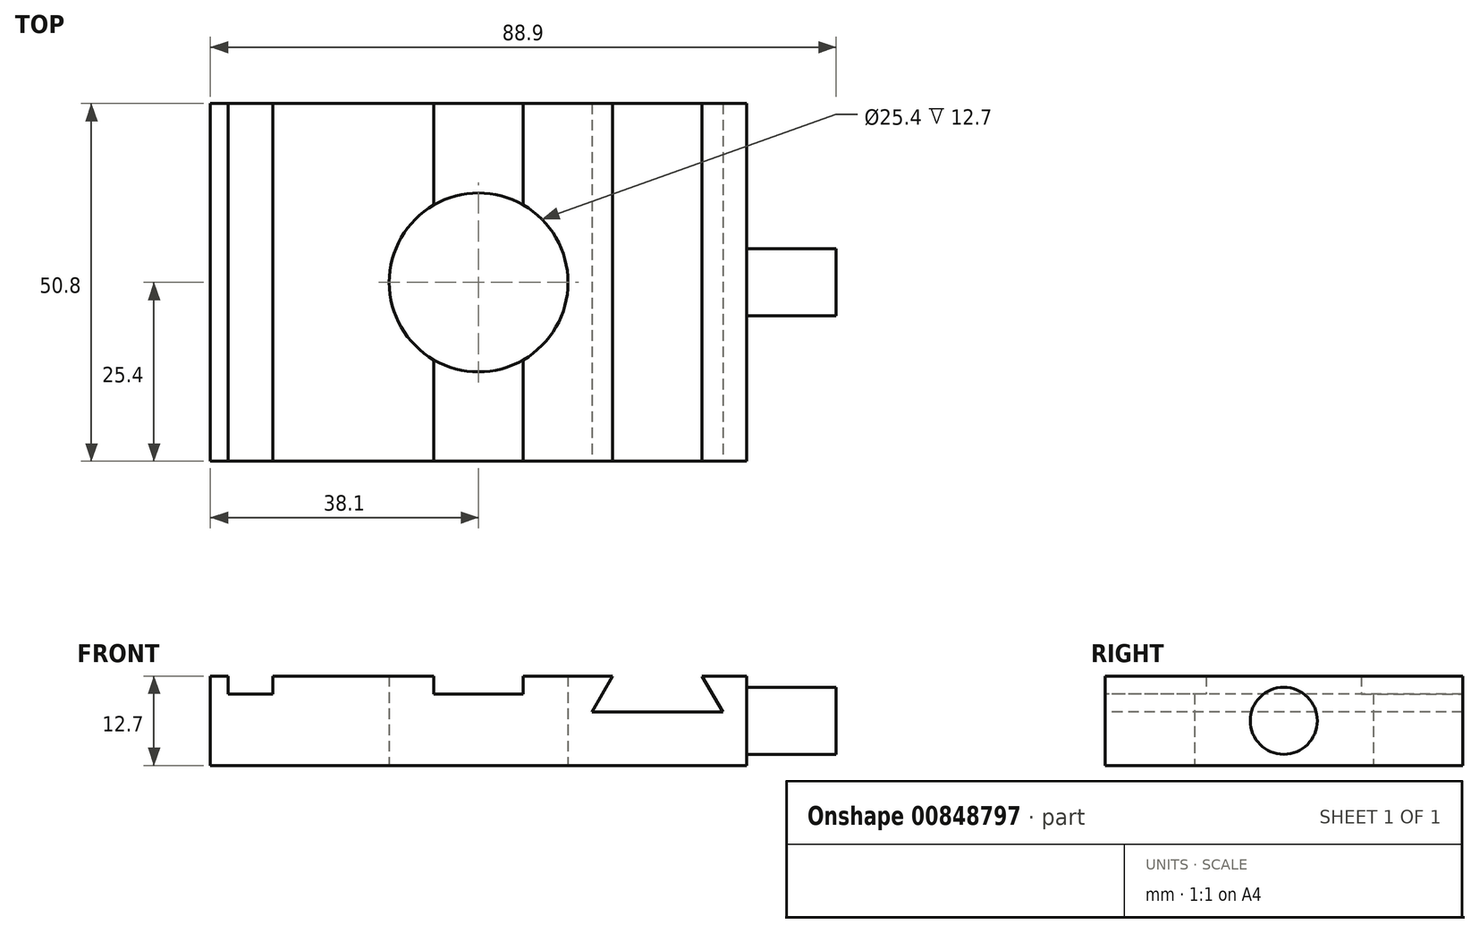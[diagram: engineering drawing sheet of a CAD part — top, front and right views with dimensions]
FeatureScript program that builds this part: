
annotation { "Feature Type Name" : "Feature", "Feature Type Description" : "" }
export const myFeature = defineFeature(function(context is Context, id is Id, definition is map)
    precondition{}
    {
        {
            var Q0;
            Q0=qCreatedBy(makeId("Top.planeOp"),FACE);
            var sketch = newSketch(context, id + "F0", { "sketchPlane" : qUnion([Q0])});
            skLineSegment(sketch, "E0.bottom", {"start": v(38.1, -25.4) * mm, "end": v(-38.1, -25.4) * mm});
            skLineSegment(sketch, "E0.top", {"start": v(38.1, 25.4) * mm, "end": v(-38.1, 25.4) * mm});
            skLineSegment(sketch, "E0.left", {"start": v(38.1, -25.4) * mm, "end": v(38.1, 25.4) * mm});
            skLineSegment(sketch, "E0.right", {"start": v(-38.1, -25.4) * mm, "end": v(-38.1, 25.4) * mm});
            skPoint(sketch, "E0.middle", {"position": v(0, 0) * mm});
            skCircle(sketch, "E1", {"center": v(0, 0) * mm, "radius": 12.7 * mm});
            skSolve(sketch);
        }
        {
            var Q0;
            Q0=makeQuery(id+"F0.imprint","IMPRINT",FACE,{"disambiguationData":[TD([[makeQuery(id+"F0.imprint","IMPRINT",EDGE,{"derivedFrom":sQuery(id+"F0.wireOp",EDGE,"E0.bottom")}),-1.0]])]});
            extrude(context, id + "F1", {"entities" : qUnion([Q0]), "depth" : 12.7 * mm, "offsetDistance" : 25 * mm});
        }
        {
            var Q0;
            Q0=makeQuery(id+"F1.opExtrude","CAP_FACE",FACE,{"disambiguationData":[OSD([sQuery(id+"F0.wireOp",EDGE,"E0.bottom"),sQuery(id+"F0.wireOp",EDGE,"E0.top"),sQuery(id+"F0.wireOp",EDGE,"E0.left"),sQuery(id+"F0.wireOp",EDGE,"E0.right"),sQuery(id+"F0.wireOp",EDGE,"E1")])],"isStart":false});
            var sketch = newSketch(context, id + "F2", { "sketchPlane" : qUnion([Q0])});
            skLineSegment(sketch, "E2.bottom", {"start": v(-35.56, 25.4) * mm, "end": v(-29.2, 25.4) * mm});
            skLineSegment(sketch, "E2.top", {"start": v(-35.56, -25.4) * mm, "end": v(-29.2, -25.4) * mm});
            skLineSegment(sketch, "E2.left", {"start": v(-35.56, 25.4) * mm, "end": v(-35.56, -25.4) * mm});
            skLineSegment(sketch, "E2.right", {"start": v(-29.2, 25.4) * mm, "end": v(-29.2, -25.4) * mm});
            skLineSegment(sketch, "E3", {"start": v(-6.35, 25.4) * mm, "end": v(-6.35, -25.4) * mm});
            skLineSegment(sketch, "E4", {"start": v(-6.35, -25.4) * mm, "end": v(6.35, -25.4) * mm});
            skLineSegment(sketch, "E5", {"start": v(6.35, -25.4) * mm, "end": v(6.35, 25.4) * mm});
            skPoint(sketch, "E6", {"position": v(0, 0) * mm});
            skLineSegment(sketch, "E7", {"start": v(0, 25.4) * mm, "end": v(0, -25.4) * mm, "construction": true});
            skSolve(sketch);
        }
        {
            var Q0;
            Q0=makeQuery(id+"F2.imprint","IMPRINT",FACE,{"disambiguationData":[TD([[makeQuery(id+"F2.imprint","IMPRINT",EDGE,{"derivedFrom":sQuery(id+"F2.wireOp",EDGE,"E2.bottom")}),1.0]])]});
            var Q1;
            {var subQ0=sQuery(id+"F2.wireOp",EDGE,"E4");Q1=makeQuery(id+"F2.imprint","IMPRINT",FACE,{"disambiguationData":[TD([[makeQuery(id+"F2.imprint","IMPRINT",EDGE,{"derivedFrom":subQ0}),-1.0]])]});}
            var Q2;
            {var subQ0=sQuery(id+"F2.wireOp",EDGE,"E3");var subQ1=makeQuery(id+"F1.opExtrude","CAP_EDGE",EDGE,{"disambiguationData":[OSD([sQuery(id+"F0.wireOp",EDGE,"E1")])],"isStart":false});var subQ2=makeQuery(id+"F2.imprint","INTERSECT",VERTEX,{"disambiguationData":[OD(0.0)],"derivedFrom":[subQ1,subQ0]});Q2=makeQuery(id+"F2.imprint","IMPRINT",FACE,{"disambiguationData":[TD([[makeQuery(id+"F2.imprint","IMPRINT",EDGE,{"disambiguationData":[TD([[subQ2,-1.0]])],"derivedFrom":subQ0}),1.0]])]});}
            var Q3;
            {var subQ0=sQuery(id+"F2.wireOp",EDGE,"E3");var subQ1=makeQuery(id+"F1.opExtrude","CAP_EDGE",EDGE,{"disambiguationData":[OSD([sQuery(id+"F0.wireOp",EDGE,"E0.top")])],"isStart":false});var subQ2=makeQuery(id+"F2.imprint","INTERSECT",VERTEX,{"derivedFrom":[subQ1,subQ0]});Q3=makeQuery(id+"F2.imprint","IMPRINT",FACE,{"disambiguationData":[TD([[makeQuery(id+"F2.imprint","IMPRINT",EDGE,{"disambiguationData":[TD([[subQ2,-1.0]])],"derivedFrom":subQ0}),1.0]])]});}
            extrude(context, id + "F3", {"entities" : qUnion([Q0, Q1, Q2, Q3]), "operationType" : NewBodyOperationType.REMOVE, "oppositeDirection" : true, "depth" : 2.54 * mm, "offsetDistance" : 25.4 * mm});
        }
        {
            var Q0;
            Q0=makeQuery(id+"F1.opExtrude","SWEPT_FACE",FACE,{"disambiguationData":[OSD([sQuery(id+"F0.wireOp",EDGE,"E0.bottom")])]});
            var sketch = newSketch(context, id + "F4", { "sketchPlane" : qUnion([Q0])});
            skLineSegment(sketch, "E8", {"start": v(19.05, 12.7) * mm, "end": v(16.12, 7.62) * mm});
            skLineSegment(sketch, "E9", {"start": v(16.12, 7.62) * mm, "end": v(34.68, 7.62) * mm});
            skLineSegment(sketch, "E10", {"start": v(34.68, 7.62) * mm, "end": v(31.75, 12.7) * mm});
            skLineSegment(sketch, "E11", {"start": v(31.75, 12.7) * mm, "end": v(19.05, 12.7) * mm});
            skLineSegment(sketch, "E12", {"start": v(25.4, 12.7) * mm, "end": v(25.4, 7.62) * mm, "construction": true});
            skSolve(sketch);
        }
        {
            var Q0;
            Q0=makeQuery(id+"F4.imprint","IMPRINT",FACE,{"disambiguationData":[TD([[makeQuery(id+"F4.imprint","IMPRINT",EDGE,{"derivedFrom":sQuery(id+"F4.wireOp",EDGE,"E8")}),1.0]])]});
            extrude(context, id + "F5", {"entities" : qUnion([Q0]), "operationType" : NewBodyOperationType.REMOVE, "endBound" : BoundingType.THROUGH_ALL, "oppositeDirection" : true, "depth" : 50.8 * mm, "offsetDistance" : 25.4 * mm});
        }
        {
            var Q0;
            Q0=makeQuery(id+"F1.opExtrude","SWEPT_FACE",FACE,{"disambiguationData":[OSD([sQuery(id+"F0.wireOp",EDGE,"E0.left")])]});
            var sketch = newSketch(context, id + "F6", { "sketchPlane" : qUnion([Q0])});
            skCircle(sketch, "E13", {"center": v(0, 6.35) * mm, "radius": 4.76 * mm});
            skPoint(sketch, "E13.centerSnap0", {"position": v(-25.4, 6.35) * mm});
            skPoint(sketch, "E13.centerSnap1", {"position": v(0, 12.7) * mm});
            skSolve(sketch);
        }
        {
            var Q0;
            Q0=makeQuery(id+"F6.imprint","IMPRINT",FACE,{"disambiguationData":[TD([[makeQuery(id+"F6.imprint","IMPRINT",EDGE,{"derivedFrom":sQuery(id+"F6.wireOp",EDGE,"E13")}),1.0]])]});
            extrude(context, id + "F7", {"entities" : qUnion([Q0]), "operationType" : NewBodyOperationType.ADD, "depth" : 12.7 * mm, "offsetDistance" : 25.4 * mm});
        }
    });
